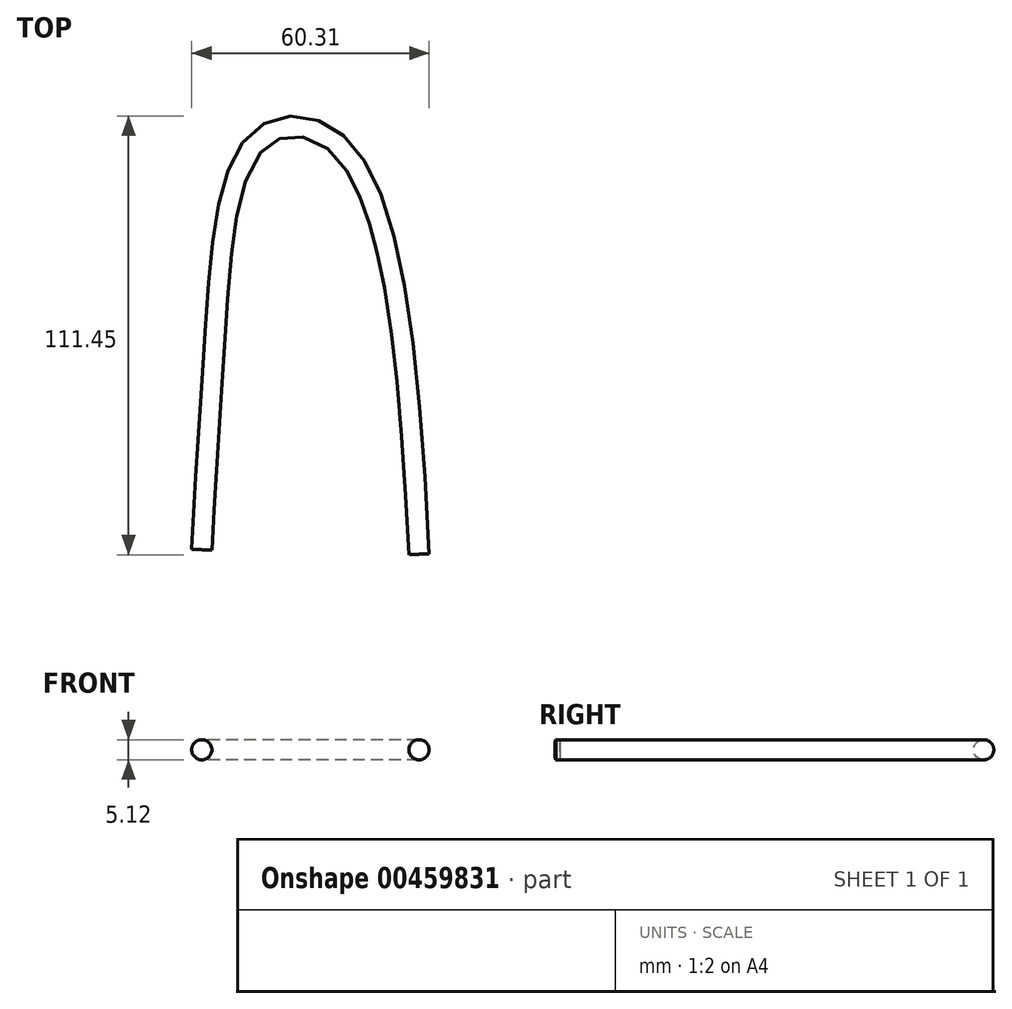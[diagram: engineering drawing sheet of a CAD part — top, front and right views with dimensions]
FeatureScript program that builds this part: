
annotation { "Feature Type Name" : "Feature", "Feature Type Description" : "" }
export const myFeature = defineFeature(function(context is Context, id is Id, definition is map)
    precondition{}
    {
        {
            var Q0;
            Q0=qCreatedBy(makeId("Top.planeOp"),FACE);
            var sketch = newSketch(context, id + "F0", { "sketchPlane" : qUnion([Q0])});
            skFitSpline(sketch, "E0", {"points": [v(-50.87, -56) * mm, v(-47.41, 0) * mm, v(-36.8, 47.74) * mm, v(-17.45, 47.82) * mm, v(4.13, -57.15) * mm], "startDerivative": vector(10.08, 210.23) * mm, "endDerivative": vector(23.12, -463.23) * mm});
            skPoint(sketch, "E1", {"position": v(-36.68, 47.85) * mm});
            skSolve(sketch);
        }
        {
            var Q0;
            Q0=sQuery(id+"F0.wireOp",EDGE,"E0");
            var Q1;
            Q1=sQuery(id+"F0.wireOp",VERTEX,"E0.start");
            cPlane(context, id + "F1", {"entities" : qUnion([Q0, Q1]), "cplaneType" : CPlaneType.CURVE_POINT, "offset" : 25 * mm, "width" : 150 * mm, "height" : 150 * mm});
        }
        {
            var Q0;
            Q0=qCreatedBy(id+"F1.planeOp",FACE);
            var sketch = newSketch(context, id + "F2", { "sketchPlane" : qUnion([Q0])});
            skCircle(sketch, "E2", {"center": v(48.23, 0) * mm, "radius": 2.56 * mm});
            skSolve(sketch);
        }
        {
            var Q0;
            Q0=makeQuery(id+"F2.imprint","IMPRINT",FACE,{"disambiguationData":[TD([[makeQuery(id+"F2.imprint","IMPRINT",EDGE,{"derivedFrom":sQuery(id+"F2.wireOp",EDGE,"E2")}),1.0]])]});
            var Q1;
            Q1=sQuery(id+"F0.wireOp",EDGE,"E0");
            sweep(context, id + "F3", {"profiles" : qUnion([Q0]), "path" : qUnion([Q1])});
        }
    });
